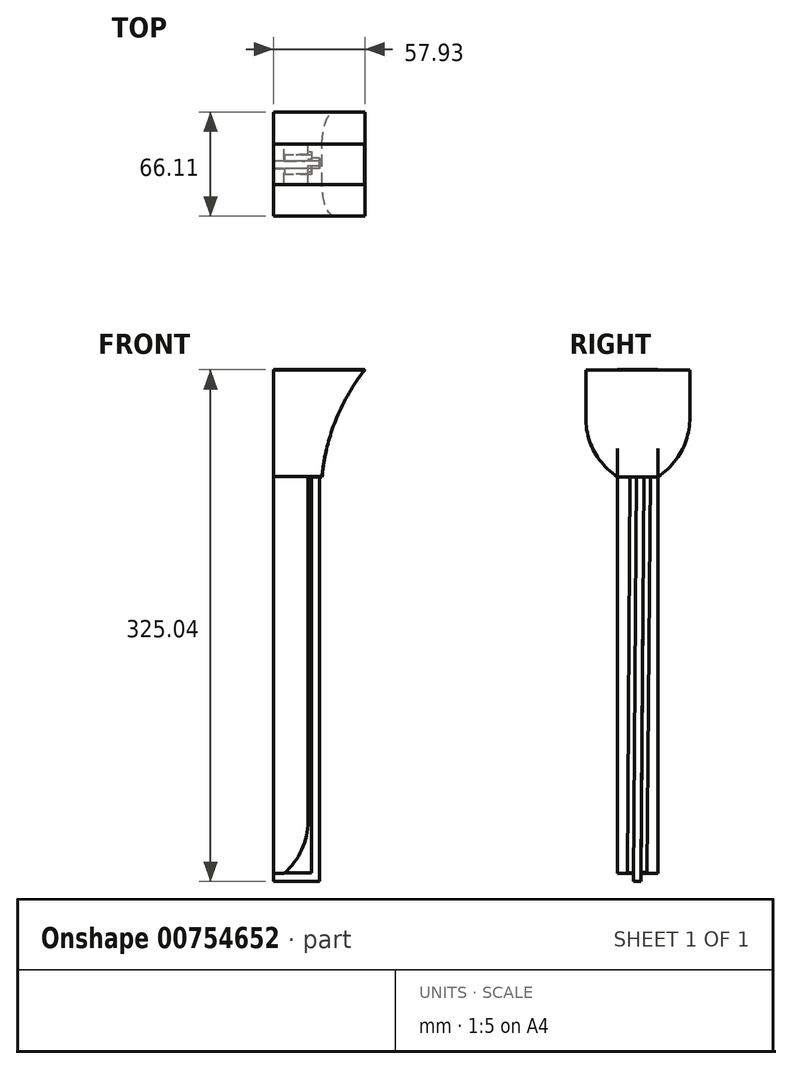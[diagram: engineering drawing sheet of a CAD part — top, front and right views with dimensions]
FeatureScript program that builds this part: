
annotation { "Feature Type Name" : "Feature", "Feature Type Description" : "" }
export const myFeature = defineFeature(function(context is Context, id is Id, definition is map)
    precondition{}
    {
        {
            var Q0;
            Q0=qCreatedBy(makeId("Front.planeOp"),FACE);
            var sketch = newSketch(context, id + "F0", { "sketchPlane" : qUnion([Q0])});
            skLineSegment(sketch, "E0", {"start": v(-17.6, 36.01) * mm, "end": v(40.28, 36.01) * mm});
            skArc(sketch, "E1", {"start": v(40.28, 36.01) * mm, "mid": v(21.73, 4) * mm, "end": v(13.24, -32.02) * mm});
            skLineSegment(sketch, "E2", {"start": v(-17.6, 36.01) * mm, "end": v(-17.6, -251.3) * mm});
            skLineSegment(sketch, "E3", {"start": v(13.24, -32.02) * mm, "end": v(4.24, -32.02) * mm});
            skLineSegment(sketch, "E4", {"start": v(4.24, -32.02) * mm, "end": v(4.24, -250.78) * mm});
            skLineSegment(sketch, "E5", {"start": v(-17.6, -251.3) * mm, "end": v(-17.6, -283.83) * mm});
            skLineSegment(sketch, "E6", {"start": v(-17.6, -283.83) * mm, "end": v(-10.96, -283.83) * mm});
            skArc(sketch, "E7", {"start": v(-10.96, -283.83) * mm, "mid": v(0.26, -268.97) * mm, "end": v(4.24, -250.78) * mm});
            skSolve(sketch);
        }
        {
            var Q0;
            Q0=makeQuery(id+"F0.imprint","IMPRINT",FACE,{"disambiguationData":[TD([[makeQuery(id+"F0.imprint","IMPRINT",EDGE,{"derivedFrom":sQuery(id+"F0.wireOp",EDGE,"E0")}),-1.0]])]});
            extrude(context, id + "F1", {"entities" : qUnion([Q0]), "depth" : 25.9 * mm, "offsetDistance" : 25.4 * mm});
        }
        {
            var Q0;
            Q0=qCreatedBy(makeId("Right.planeOp"),FACE);
            var sketch = newSketch(context, id + "F2", { "sketchPlane" : qUnion([Q0])});
            skLineSegment(sketch, "E8", {"start": v(-17.78, -32.08) * mm, "end": v(-19.4, -283.52) * mm});
            skLineSegment(sketch, "E9", {"start": v(-19.4, -283.52) * mm, "end": v(-14.7, -283.55) * mm});
            skLineSegment(sketch, "E10", {"start": v(-14.7, -283.55) * mm, "end": v(-13.1, -32.08) * mm});
            skLineSegment(sketch, "E11", {"start": v(-13.1, -32.08) * mm, "end": v(-17.78, -32.08) * mm});
            skSolve(sketch);
        }
        {
            var Q0;
            Q0=makeQuery(id+"F2.imprint","IMPRINT",FACE,{"disambiguationData":[TD([[makeQuery(id+"F2.imprint","IMPRINT",EDGE,{"derivedFrom":sQuery(id+"F2.wireOp",EDGE,"E8")}),1.0]])]});
            extrude(context, id + "F3", {"entities" : qUnion([Q0]), "operationType" : NewBodyOperationType.ADD, "depth" : 6.6 * mm, "offsetDistance" : 25.4 * mm});
        }
        {
            var Q0;
            Q0=qCreatedBy(makeId("Right.planeOp"),FACE);
            var sketch = newSketch(context, id + "F4", { "sketchPlane" : qUnion([Q0])});
            skLineSegment(sketch, "E12", {"start": v(-13.39, 8.56) * mm, "end": v(-15.68, -289.03) * mm});
            skLineSegment(sketch, "E13", {"start": v(-15.68, -289.03) * mm, "end": v(-11, -289.03) * mm});
            skLineSegment(sketch, "E14", {"start": v(-11, -289.03) * mm, "end": v(-8.7, 8.52) * mm});
            skLineSegment(sketch, "E15", {"start": v(-8.7, 8.52) * mm, "end": v(-13.39, 8.56) * mm});
            skSolve(sketch);
        }
        {
            var Q0;
            Q0=makeQuery(id+"F4.imprint","IMPRINT",FACE,{"disambiguationData":[TD([[makeQuery(id+"F4.imprint","IMPRINT",EDGE,{"derivedFrom":sQuery(id+"F4.wireOp",EDGE,"E12")}),1.0]])]});
            extrude(context, id + "F5", {"entities" : qUnion([Q0]), "operationType" : NewBodyOperationType.ADD, "depth" : 11.68 * mm, "offsetDistance" : 25.4 * mm});
        }
        {
            var Q0;
            Q0=qCreatedBy(makeId("Right.planeOp"),FACE);
            var sketch = newSketch(context, id + "F6", { "sketchPlane" : qUnion([Q0])});
            skLineSegment(sketch, "E16", {"start": v(-9.03, -32) * mm, "end": v(-5.01, -32) * mm});
            skLineSegment(sketch, "E17", {"start": v(-5.01, -32) * mm, "end": v(-7.07, -283.43) * mm});
            skLineSegment(sketch, "E18", {"start": v(-7.07, -283.43) * mm, "end": v(-10.91, -283.43) * mm});
            skLineSegment(sketch, "E19", {"start": v(-10.91, -283.43) * mm, "end": v(-9.03, -32) * mm});
            skSolve(sketch);
        }
        {
            var Q0;
            Q0=makeQuery(id+"F6.imprint","IMPRINT",FACE,{"disambiguationData":[TD([[makeQuery(id+"F6.imprint","IMPRINT",EDGE,{"derivedFrom":sQuery(id+"F6.wireOp",EDGE,"E16")}),-1.0]])]});
            extrude(context, id + "F7", {"entities" : qUnion([Q0]), "operationType" : NewBodyOperationType.ADD, "depth" : 6.6 * mm, "offsetDistance" : 25.4 * mm});
        }
        {
            var Q0;
            Q0=qCreatedBy(makeId("Front.planeOp"),FACE);
            var sketch = newSketch(context, id + "F8", { "sketchPlane" : qUnion([Q0])});
            skLineSegment(sketch, "E20", {"start": v(13.1, -31.95) * mm, "end": v(-17.6, -31.95) * mm});
            skLineSegment(sketch, "E21", {"start": v(-17.6, -31.95) * mm, "end": v(-17.6, 35.95) * mm});
            skLineSegment(sketch, "E22", {"start": v(-17.6, 35.95) * mm, "end": v(40.33, 35.95) * mm});
            skArc(sketch, "E23", {"start": v(40.33, 35.95) * mm, "mid": v(21.8, 3.97) * mm, "end": v(13.1, -31.95) * mm});
            skSolve(sketch);
        }
        {
            var Q0;
            Q0=makeQuery(id+"F8.imprint","IMPRINT",FACE,{"disambiguationData":[TD([[makeQuery(id+"F8.imprint","IMPRINT",EDGE,{"derivedFrom":sQuery(id+"F8.wireOp",EDGE,"E20")}),-1.0]])]});
            extrude(context, id + "F9", {"entities" : qUnion([Q0]), "operationType" : NewBodyOperationType.ADD, "oppositeDirection" : true, "depth" : 20.14 * mm, "offsetDistance" : 25.4 * mm});
        }
        {
            var Q0;
            Q0=makeQuery(id+"F8.imprint","IMPRINT",FACE,{"disambiguationData":[TD([[makeQuery(id+"F8.imprint","IMPRINT",EDGE,{"derivedFrom":sQuery(id+"F8.wireOp",EDGE,"E20")}),-1.0]])]});
            extrude(context, id + "F10", {"entities" : qUnion([Q0]), "operationType" : NewBodyOperationType.ADD, "depth" : 45.97 * mm, "offsetDistance" : 25.4 * mm});
        }
        {
            var Q0;
            Q0=makeQuery(id+"F7.opExtrude","CAP_FACE",FACE,{"disambiguationData":[OSD([sQuery(id+"F6.wireOp",EDGE,"E16"),sQuery(id+"F6.wireOp",EDGE,"E17"),sQuery(id+"F6.wireOp",EDGE,"E18"),sQuery(id+"F6.wireOp",EDGE,"E19")])],"isStart":true});
            extrude(context, id + "F11", {"entities" : qUnion([Q0]), "operationType" : NewBodyOperationType.ADD, "depth" : 10.92 * mm, "offsetDistance" : 25.4 * mm});
        }
        {
            var Q0;
            Q0=makeQuery(id+"F5.boolean.opBoolean","MERGE",FACE,{"derivedFrom":[makeQuery(id+"F3.opExtrude","CAP_FACE",FACE,{"disambiguationData":[OSD([sQuery(id+"F2.wireOp",EDGE,"E8"),sQuery(id+"F2.wireOp",EDGE,"E9"),sQuery(id+"F2.wireOp",EDGE,"E10"),sQuery(id+"F2.wireOp",EDGE,"E11")])],"isStart":true}),makeQuery(id+"F5.opExtrude","CAP_FACE",FACE,{"disambiguationData":[OSD([sQuery(id+"F4.wireOp",EDGE,"E12"),sQuery(id+"F4.wireOp",EDGE,"E13"),sQuery(id+"F4.wireOp",EDGE,"E14"),sQuery(id+"F4.wireOp",EDGE,"E15")])],"isStart":true})]});
            extrude(context, id + "F12", {"entities" : qUnion([Q0]), "operationType" : NewBodyOperationType.ADD, "depth" : 17.6 * mm, "offsetDistance" : 25.4 * mm});
        }
        {
            var Q0;
            Q0=makeQuery(id+"F9.opExtrude","CAP_EDGE",EDGE,{"disambiguationData":[OSD([sQuery(id+"F8.wireOp",EDGE,"E20")])],"isStart":false});
            fillet(context, id + "F13", {"entities" : qUnion([Q0]), "radius" : 44.76 * mm, "tangentPropagation" : true, "allowEdgeOverflow" : false});
        }
        {
            var Q0;
            Q0=makeQuery(id+"F10.opExtrude","CAP_EDGE",EDGE,{"disambiguationData":[OSD([sQuery(id+"F8.wireOp",EDGE,"E20")])],"isStart":false});
            fillet(context, id + "F14", {"entities" : qUnion([Q0]), "radius" : 44.75 * mm, "tangentPropagation" : true, "allowEdgeOverflow" : false});
        }
    });
